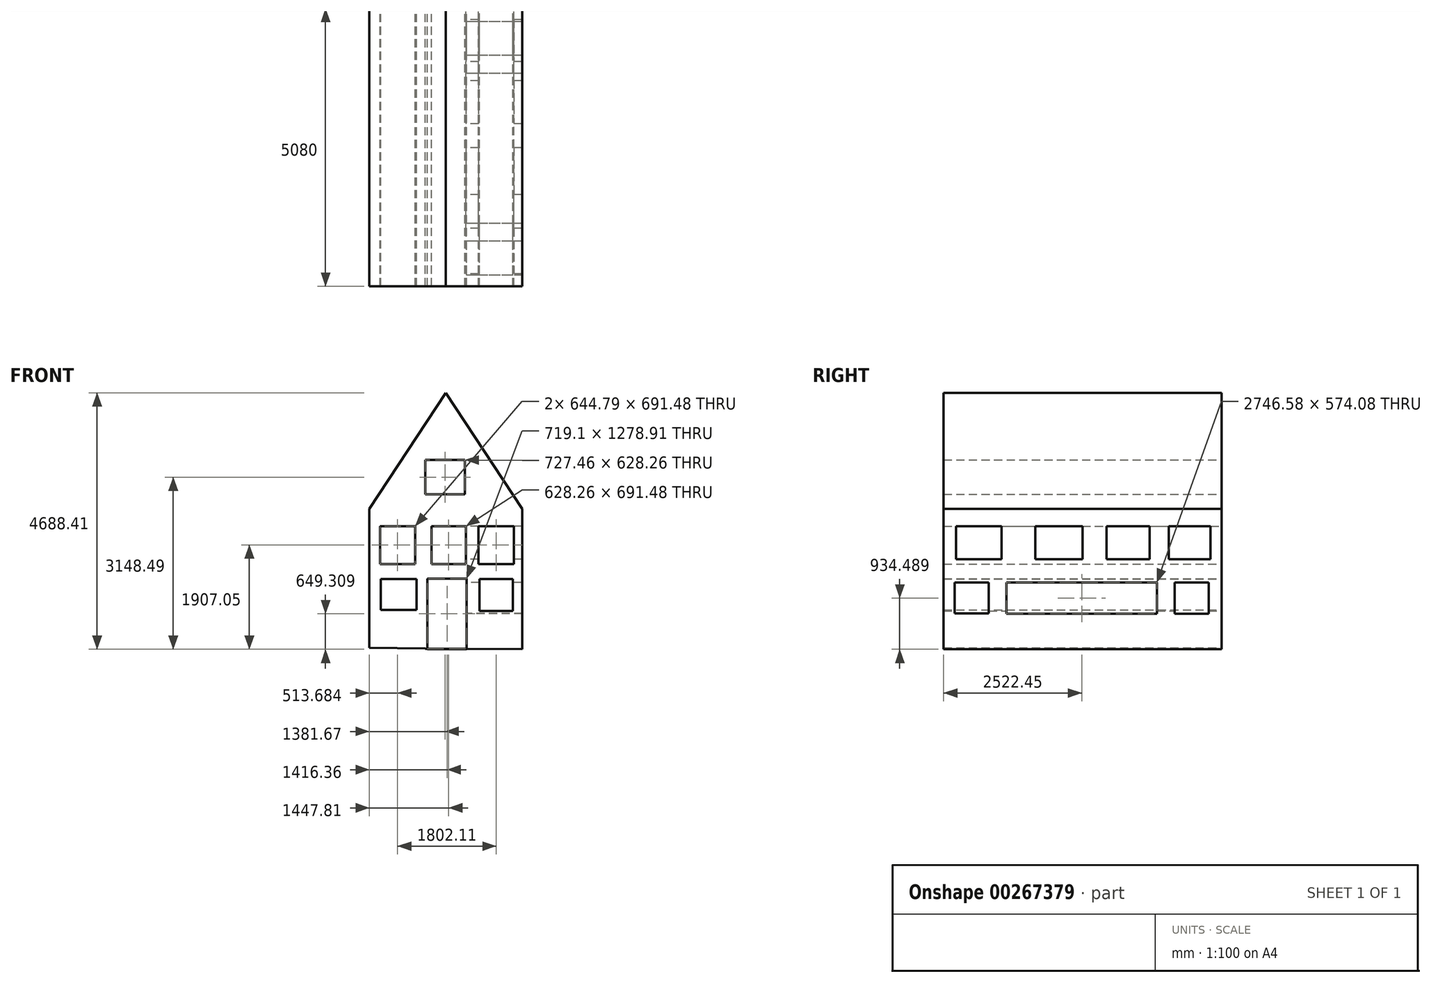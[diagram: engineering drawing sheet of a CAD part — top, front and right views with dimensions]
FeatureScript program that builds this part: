
annotation { "Feature Type Name" : "Feature", "Feature Type Description" : "" }
export const myFeature = defineFeature(function(context is Context, id is Id, definition is map)
    precondition{}
    {
        {
            var Q0;
            Q0=qCreatedBy(makeId("Front.planeOp"),FACE);
            var sketch = newSketch(context, id + "F0", { "sketchPlane" : qUnion([Q0])});
            skLineSegment(sketch, "E0", {"start": v(-1301.24, 314.26) * mm, "end": v(-1301.24, -2225.74) * mm});
            skLineSegment(sketch, "E1", {"start": v(-1301.24, 314.26) * mm, "end": v(1492.62, 314.26) * mm});
            skLineSegment(sketch, "E2", {"start": v(1492.62, -2252.8) * mm, "end": v(-1301.24, -2225.74) * mm});
            skLineSegment(sketch, "E3", {"start": v(1492.62, 314.26) * mm, "end": v(1492.62, -2252.8) * mm});
            skLineSegment(sketch, "E4", {"start": v(-1301.24, 314.26) * mm, "end": v(95.7, 2435.62) * mm});
            skPoint(sketch, "E4.endSnap0", {"position": v(95.7, 314.26) * mm});
            skLineSegment(sketch, "E5", {"start": v(95.7, 2435.62) * mm, "end": v(1492.62, 314.26) * mm});
            skLineSegment(sketch, "E6.bottom", {"start": v(-283.3, -873.34) * mm, "end": v(493.62, -873.34) * mm});
            skLineSegment(sketch, "E6.top", {"start": v(-283.3, -2243.12) * mm, "end": v(493.62, -2243.12) * mm});
            skLineSegment(sketch, "E6.left", {"start": v(-283.3, -873.34) * mm, "end": v(-283.3, -2243.12) * mm});
            skLineSegment(sketch, "E6.right", {"start": v(493.62, -873.34) * mm, "end": v(493.62, -2243.12) * mm});
            skPoint(sketch, "E7.firstSnap0", {"position": v(1492.62, -969.27) * mm});
            skLineSegment(sketch, "E7.bottom", {"start": v(708.7, -969.27) * mm, "end": v(1320.42, -969.27) * mm});
            skLineSegment(sketch, "E7.top", {"start": v(708.7, -1551.2) * mm, "end": v(1320.42, -1551.2) * mm});
            skLineSegment(sketch, "E7.left", {"start": v(708.7, -969.27) * mm, "end": v(708.7, -1551.2) * mm});
            skLineSegment(sketch, "E7.right", {"start": v(1320.42, -969.27) * mm, "end": v(1320.42, -1551.2) * mm});
            skLineSegment(sketch, "E8.bottom", {"start": v(-1093.42, -969.27) * mm, "end": v(-438.03, -969.27) * mm});
            skLineSegment(sketch, "E8.top", {"start": v(-1093.42, -1534.67) * mm, "end": v(-438.03, -1534.67) * mm});
            skLineSegment(sketch, "E8.left", {"start": v(-1093.42, -969.27) * mm, "end": v(-1093.42, -1534.67) * mm});
            skLineSegment(sketch, "E8.right", {"start": v(-438.03, -969.27) * mm, "end": v(-438.03, -1534.67) * mm});
            skLineSegment(sketch, "E9.bottom", {"start": v(-283.3, 1209.83) * mm, "end": v(444.16, 1209.83) * mm});
            skLineSegment(sketch, "E9.top", {"start": v(-283.3, 581.57) * mm, "end": v(444.16, 581.57) * mm});
            skLineSegment(sketch, "E9.left", {"start": v(-283.3, 1209.83) * mm, "end": v(-283.3, 581.57) * mm});
            skLineSegment(sketch, "E9.right", {"start": v(444.16, 1209.83) * mm, "end": v(444.16, 581.57) * mm});
            skLineSegment(sketch, "E10", {"start": v(-1093.42, -1251.97) * mm, "end": v(-438.03, -1251.97) * mm});
            skLineSegment(sketch, "E11", {"start": v(708.7, -1260.23) * mm, "end": v(1320.42, -1260.23) * mm});
            skLineSegment(sketch, "E12", {"start": v(-283.3, 895.7) * mm, "end": v(444.16, 895.7) * mm});
            skLineSegment(sketch, "E13", {"start": v(80.43, 1209.83) * mm, "end": v(80.43, 581.57) * mm});
            skLineSegment(sketch, "E14", {"start": v(1014.55, -969.27) * mm, "end": v(1014.55, -1551.2) * mm});
            skLineSegment(sketch, "E15", {"start": v(-765.72, -969.27) * mm, "end": v(-765.72, -1534.67) * mm});
            skLineSegment(sketch, "E16.bottom", {"start": v(-1109.95, 0) * mm, "end": v(-465.16, 0) * mm});
            skLineSegment(sketch, "E16.top", {"start": v(-1109.95, -691.48) * mm, "end": v(-465.16, -691.48) * mm});
            skLineSegment(sketch, "E16.left", {"start": v(-1109.95, 0) * mm, "end": v(-1109.95, -691.48) * mm});
            skLineSegment(sketch, "E16.right", {"start": v(-465.16, 0) * mm, "end": v(-465.16, -691.48) * mm});
            skLineSegment(sketch, "E17.bottom", {"start": v(-167.56, 0) * mm, "end": v(460.7, 0) * mm});
            skLineSegment(sketch, "E17.top", {"start": v(-167.56, -691.48) * mm, "end": v(460.7, -691.48) * mm});
            skLineSegment(sketch, "E17.left", {"start": v(-167.56, 0) * mm, "end": v(-167.56, -691.48) * mm});
            skLineSegment(sketch, "E17.right", {"start": v(460.7, 0) * mm, "end": v(460.7, -691.48) * mm});
            skLineSegment(sketch, "E18.bottom", {"start": v(692.16, 0) * mm, "end": v(1336.95, 0) * mm});
            skLineSegment(sketch, "E18.top", {"start": v(692.16, -691.48) * mm, "end": v(1336.95, -691.48) * mm});
            skLineSegment(sketch, "E18.left", {"start": v(692.16, 0) * mm, "end": v(692.16, -691.48) * mm});
            skLineSegment(sketch, "E18.right", {"start": v(1336.95, 0) * mm, "end": v(1336.95, -691.48) * mm});
            skLineSegment(sketch, "E19", {"start": v(-1109.95, -345.74) * mm, "end": v(-465.16, -345.74) * mm});
            skLineSegment(sketch, "E20", {"start": v(-787.56, 0) * mm, "end": v(-787.56, -691.48) * mm});
            skLineSegment(sketch, "E21", {"start": v(-167.56, -345.74) * mm, "end": v(460.7, -345.74) * mm});
            skLineSegment(sketch, "E22", {"start": v(146.57, 0) * mm, "end": v(146.57, -691.48) * mm});
            skLineSegment(sketch, "E23", {"start": v(692.16, -345.74) * mm, "end": v(1336.95, -345.74) * mm});
            skLineSegment(sketch, "E24", {"start": v(1014.55, 0) * mm, "end": v(1014.55, -691.48) * mm});
            skLineSegment(sketch, "E25.bottom", {"start": v(-244.44, -964.03) * mm, "end": v(474.67, -964.03) * mm});
            skLineSegment(sketch, "E25.top", {"start": v(-244.44, -2247.35) * mm, "end": v(474.67, -2247.35) * mm});
            skLineSegment(sketch, "E25.left", {"start": v(-244.44, -964.03) * mm, "end": v(-244.44, -2247.35) * mm});
            skLineSegment(sketch, "E25.right", {"start": v(474.67, -964.03) * mm, "end": v(474.67, -2247.35) * mm});
            skSolve(sketch);
        }
        {
            var Q0;
            Q0 = qSketchRegion(id + "F0", true);
            extrude(context, id + "F1", {"entities" : qUnion([Q0]), "depth" : 5080 * mm});
        }
        {
            var Q0;
            Q0=qCreatedBy(makeId("Right.planeOp"),FACE);
            var sketch = newSketch(context, id + "F2", { "sketchPlane" : qUnion([Q0])});
            skLineSegment(sketch, "E26.bottom", {"start": v(-238.71, -1031.26) * mm, "end": v(-857.82, -1031.26) * mm});
            skLineSegment(sketch, "E26.top", {"start": v(-238.71, -1605.34) * mm, "end": v(-857.82, -1605.34) * mm});
            skLineSegment(sketch, "E26.left", {"start": v(-238.71, -1031.26) * mm, "end": v(-238.71, -1605.34) * mm});
            skLineSegment(sketch, "E26.right", {"start": v(-857.82, -1031.26) * mm, "end": v(-857.82, -1605.34) * mm});
            skLineSegment(sketch, "E27.bottom", {"start": v(-1184.26, -1031.26) * mm, "end": v(-3930.84, -1031.26) * mm});
            skLineSegment(sketch, "E27.top", {"start": v(-1184.26, -1605.34) * mm, "end": v(-3930.84, -1605.34) * mm});
            skLineSegment(sketch, "E27.left", {"start": v(-1184.26, -1031.26) * mm, "end": v(-1184.26, -1605.34) * mm});
            skLineSegment(sketch, "E27.right", {"start": v(-3930.84, -1031.26) * mm, "end": v(-3930.84, -1605.34) * mm});
            skLineSegment(sketch, "E28.bottom", {"start": v(-4257.28, -1031.26) * mm, "end": v(-4876.38, -1031.26) * mm});
            skLineSegment(sketch, "E28.top", {"start": v(-4257.28, -1594.09) * mm, "end": v(-4876.38, -1594.09) * mm});
            skLineSegment(sketch, "E28.left", {"start": v(-4257.28, -1031.26) * mm, "end": v(-4257.28, -1594.09) * mm});
            skLineSegment(sketch, "E28.right", {"start": v(-4876.38, -1031.26) * mm, "end": v(-4876.38, -1594.09) * mm});
            skLineSegment(sketch, "E29.bottom", {"start": v(-3404.75, 0) * mm, "end": v(-2545.12, 0) * mm});
            skLineSegment(sketch, "E29.top", {"start": v(-3404.75, -603.51) * mm, "end": v(-2545.12, -603.51) * mm});
            skLineSegment(sketch, "E29.left", {"start": v(-3404.75, 0) * mm, "end": v(-3404.75, -603.51) * mm});
            skLineSegment(sketch, "E29.right", {"start": v(-2545.12, 0) * mm, "end": v(-2545.12, -603.51) * mm});
            skLineSegment(sketch, "E30.bottom", {"start": v(-4853.87, 0) * mm, "end": v(-4020.9, 0) * mm});
            skLineSegment(sketch, "E30.top", {"start": v(-4853.87, -603.51) * mm, "end": v(-4020.9, -603.51) * mm});
            skLineSegment(sketch, "E30.left", {"start": v(-4853.87, 0) * mm, "end": v(-4853.87, -603.51) * mm});
            skLineSegment(sketch, "E30.right", {"start": v(-4020.9, 0) * mm, "end": v(-4020.9, -603.51) * mm});
            skPoint(sketch, "E31.oppositeSnap0", {"position": v(-2974.93, -603.51) * mm});
            skLineSegment(sketch, "E31.bottom", {"start": v(-2107.29, 0) * mm, "end": v(-1319.33, 0) * mm});
            skLineSegment(sketch, "E31.top", {"start": v(-2107.29, -603.51) * mm, "end": v(-1319.33, -603.51) * mm});
            skLineSegment(sketch, "E31.left", {"start": v(-2107.29, 0) * mm, "end": v(-2107.29, -603.51) * mm});
            skLineSegment(sketch, "E31.right", {"start": v(-1319.33, 0) * mm, "end": v(-1319.33, -603.51) * mm});
            skLineSegment(sketch, "E32.bottom", {"start": v(-970.38, 0) * mm, "end": v(-204.94, 0) * mm});
            skLineSegment(sketch, "E32.top", {"start": v(-970.38, -603.51) * mm, "end": v(-204.94, -603.51) * mm});
            skLineSegment(sketch, "E32.left", {"start": v(-970.38, 0) * mm, "end": v(-970.38, -603.51) * mm});
            skLineSegment(sketch, "E32.right", {"start": v(-204.94, 0) * mm, "end": v(-204.94, -603.51) * mm});
            skSolve(sketch);
        }
        {
            var Q0;
            Q0 = qSketchRegion(id + "F2", true);
            extrude(context, id + "F3", {"entities" : qUnion([Q0]), "operationType" : NewBodyOperationType.REMOVE, "depth" : 22860 * mm});
        }
    });
